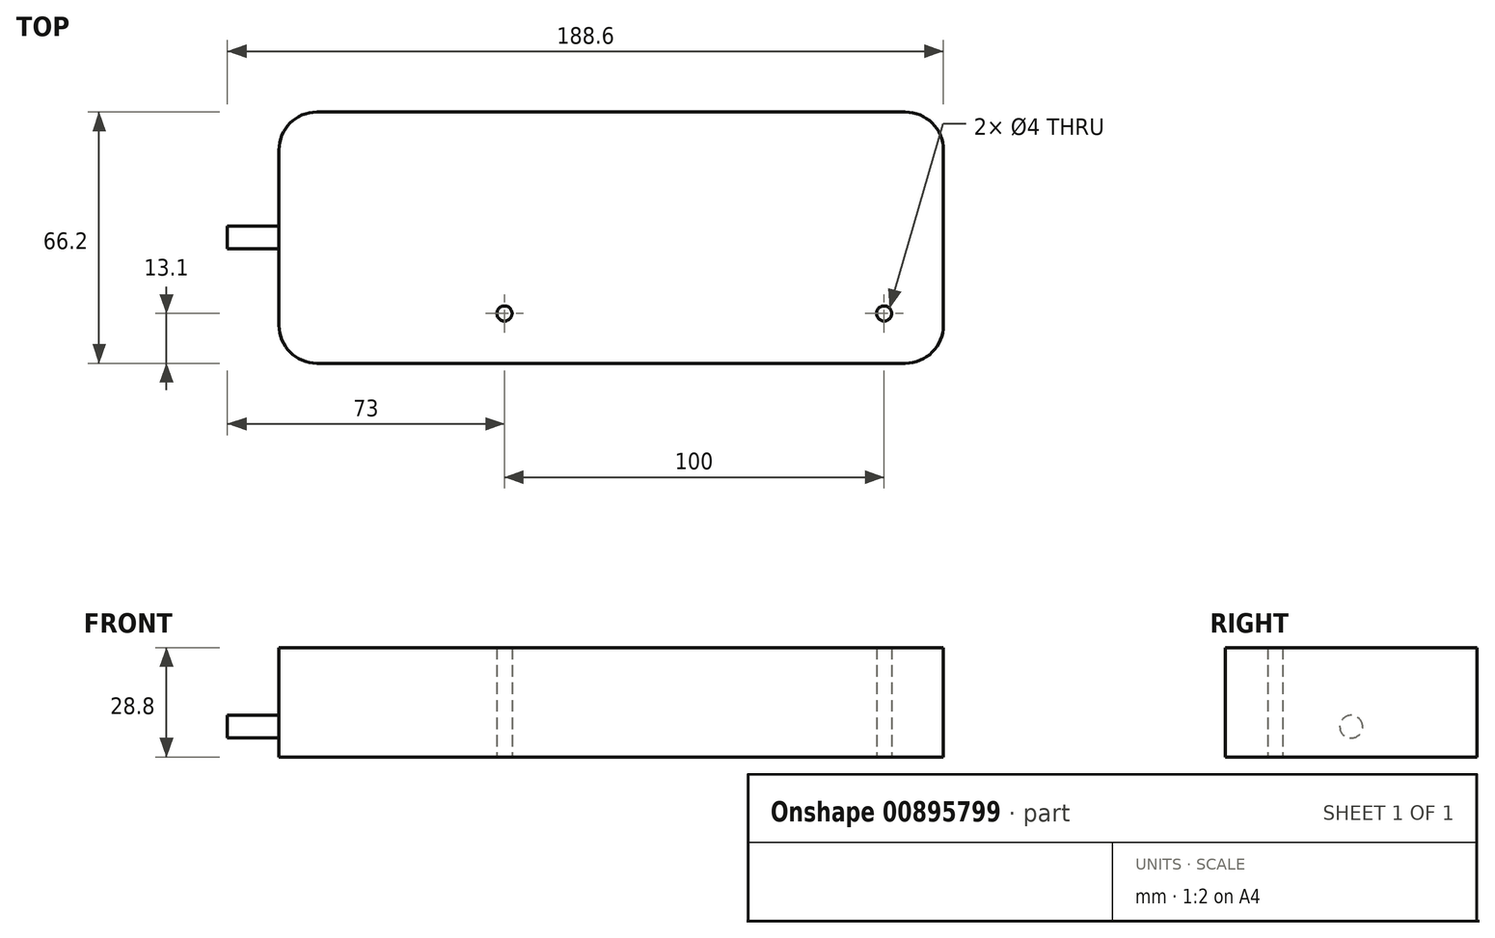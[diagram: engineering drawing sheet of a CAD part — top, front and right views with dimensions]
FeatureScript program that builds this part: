
annotation { "Feature Type Name" : "Feature", "Feature Type Description" : "" }
export const myFeature = defineFeature(function(context is Context, id is Id, definition is map)
    precondition{}
    {
        {
            var Q0;
            Q0=qCreatedBy(makeId("Top.planeOp"),FACE);
            var sketch = newSketch(context, id + "F0", { "sketchPlane" : qUnion([Q0])});
            skLineSegment(sketch, "E0.bottom", {"start": v(-77.5, 33.1) * mm, "end": v(77.5, 33.1) * mm});
            skLineSegment(sketch, "E0.top", {"start": v(-77.5, -33.1) * mm, "end": v(77.5, -33.1) * mm});
            skLineSegment(sketch, "E0.left", {"start": v(-87.5, 23.1) * mm, "end": v(-87.5, -23.1) * mm});
            skLineSegment(sketch, "E0.right", {"start": v(87.5, 23.1) * mm, "end": v(87.5, -23.1) * mm});
            skPoint(sketch, "E0.middle", {"position": v(0, 0) * mm});
            skCircle(sketch, "E1", {"center": v(-28.1, 20) * mm, "radius": 2 * mm});
            skCircle(sketch, "E2", {"center": v(71.9, 20) * mm, "radius": 2 * mm});
            skCircle(sketch, "E3.MirrorC", {"center": v(-28.1, -20) * mm, "radius": 2 * mm});
            skCircle(sketch, "E4.MirrorC", {"center": v(71.9, -20) * mm, "radius": 2 * mm});
            skPoint(sketch, "E5.visualSharp", {"position": v(87.5, 33.1) * mm});
            skArc(sketch, "E5.filletArc", {"start": v(87.5, 23.1) * mm, "mid": v(84.57, 30.17) * mm, "end": v(77.5, 33.1) * mm});
            skPoint(sketch, "E6.visualSharp", {"position": v(87.5, -33.1) * mm});
            skArc(sketch, "E6.filletArc", {"start": v(77.5, -33.1) * mm, "mid": v(84.57, -30.17) * mm, "end": v(87.5, -23.1) * mm});
            skPoint(sketch, "E7.visualSharp", {"position": v(-87.5, 33.1) * mm});
            skArc(sketch, "E7.filletArc", {"start": v(-77.5, 33.1) * mm, "mid": v(-84.57, 30.17) * mm, "end": v(-87.5, 23.1) * mm});
            skPoint(sketch, "E8.visualSharp", {"position": v(-87.5, -33.1) * mm});
            skArc(sketch, "E8.filletArc", {"start": v(-87.5, -23.1) * mm, "mid": v(-84.57, -30.17) * mm, "end": v(-77.5, -33.1) * mm});
            skSolve(sketch);
        }
        {
            var Q0;
            Q0 = qSketchRegion(id + "F0", true);
            var Q1;
            Q1=makeQuery(id+"F0.imprint","IMPRINT",FACE,{"disambiguationData":[TD([[makeQuery(id+"F0.imprint","IMPRINT",EDGE,{"derivedFrom":sQuery(id+"F0.wireOp",EDGE,"E1")}),1.0]])]});
            var Q2;
            Q2=makeQuery(id+"F0.imprint","IMPRINT",FACE,{"disambiguationData":[TD([[makeQuery(id+"F0.imprint","IMPRINT",EDGE,{"derivedFrom":sQuery(id+"F0.wireOp",EDGE,"E3.MirrorC")}),-1.0]])]});
            var Q3;
            Q3=makeQuery(id+"F0.imprint","IMPRINT",FACE,{"disambiguationData":[TD([[makeQuery(id+"F0.imprint","IMPRINT",EDGE,{"derivedFrom":sQuery(id+"F0.wireOp",EDGE,"E2")}),1.0]])]});
            var Q4;
            Q4=makeQuery(id+"F0.imprint","IMPRINT",FACE,{"disambiguationData":[TD([[makeQuery(id+"F0.imprint","IMPRINT",EDGE,{"derivedFrom":sQuery(id+"F0.wireOp",EDGE,"E4.MirrorC")}),-1.0]])]});
            extrude(context, id + "F1", {"entities" : qUnion([Q0, Q1, Q2, Q3, Q4]), "depth" : 32.8 * mm, "offsetDistance" : 25 * mm});
        }
        {
            var Q0;
            Q0=makeQuery(id+"F1.opExtrude","SWEPT_FACE",FACE,{"disambiguationData":[OSD([sQuery(id+"F0.wireOp",EDGE,"E0.left")])]});
            var sketch = newSketch(context, id + "F2", { "sketchPlane" : qUnion([Q0])});
            skCircle(sketch, "E9", {"center": v(0, 12) * mm, "radius": 3 * mm});
            skPoint(sketch, "E9.centerSnap0", {"position": v(-23.1, 12) * mm});
            skPoint(sketch, "E9.centerSnap1", {"position": v(0, 32.8) * mm});
            skSolve(sketch);
        }
        {
            var Q0;
            Q0 = qSketchRegion(id + "F2", true);
            extrude(context, id + "F3", {"entities" : qUnion([Q0]), "operationType" : NewBodyOperationType.ADD, "depth" : 13.6 * mm, "offsetDistance" : 25 * mm});
        }
        {
            var Q0;
            Q0=makeQuery(id+"F0.imprint","IMPRINT",FACE,{"disambiguationData":[TD([[makeQuery(id+"F0.imprint","IMPRINT",EDGE,{"derivedFrom":sQuery(id+"F0.wireOp",EDGE,"E3.MirrorC")}),-1.0]])]});
            var Q1;
            Q1=makeQuery(id+"F0.imprint","IMPRINT",FACE,{"disambiguationData":[TD([[makeQuery(id+"F0.imprint","IMPRINT",EDGE,{"derivedFrom":sQuery(id+"F0.wireOp",EDGE,"E1")}),1.0]])]});
            var Q2;
            Q2=makeQuery(id+"F0.imprint","IMPRINT",FACE,{"disambiguationData":[TD([[makeQuery(id+"F0.imprint","IMPRINT",EDGE,{"derivedFrom":sQuery(id+"F0.wireOp",EDGE,"E2")}),1.0]])]});
            var Q3;
            Q3=makeQuery(id+"F0.imprint","IMPRINT",FACE,{"disambiguationData":[TD([[makeQuery(id+"F0.imprint","IMPRINT",EDGE,{"derivedFrom":sQuery(id+"F0.wireOp",EDGE,"E4.MirrorC")}),-1.0]])]});
            extrude(context, id + "F4", {"entities" : qUnion([Q0, Q1, Q2, Q3]), "operationType" : NewBodyOperationType.REMOVE, "depth" : 4 * mm, "offsetDistance" : 25 * mm});
        }
    });
